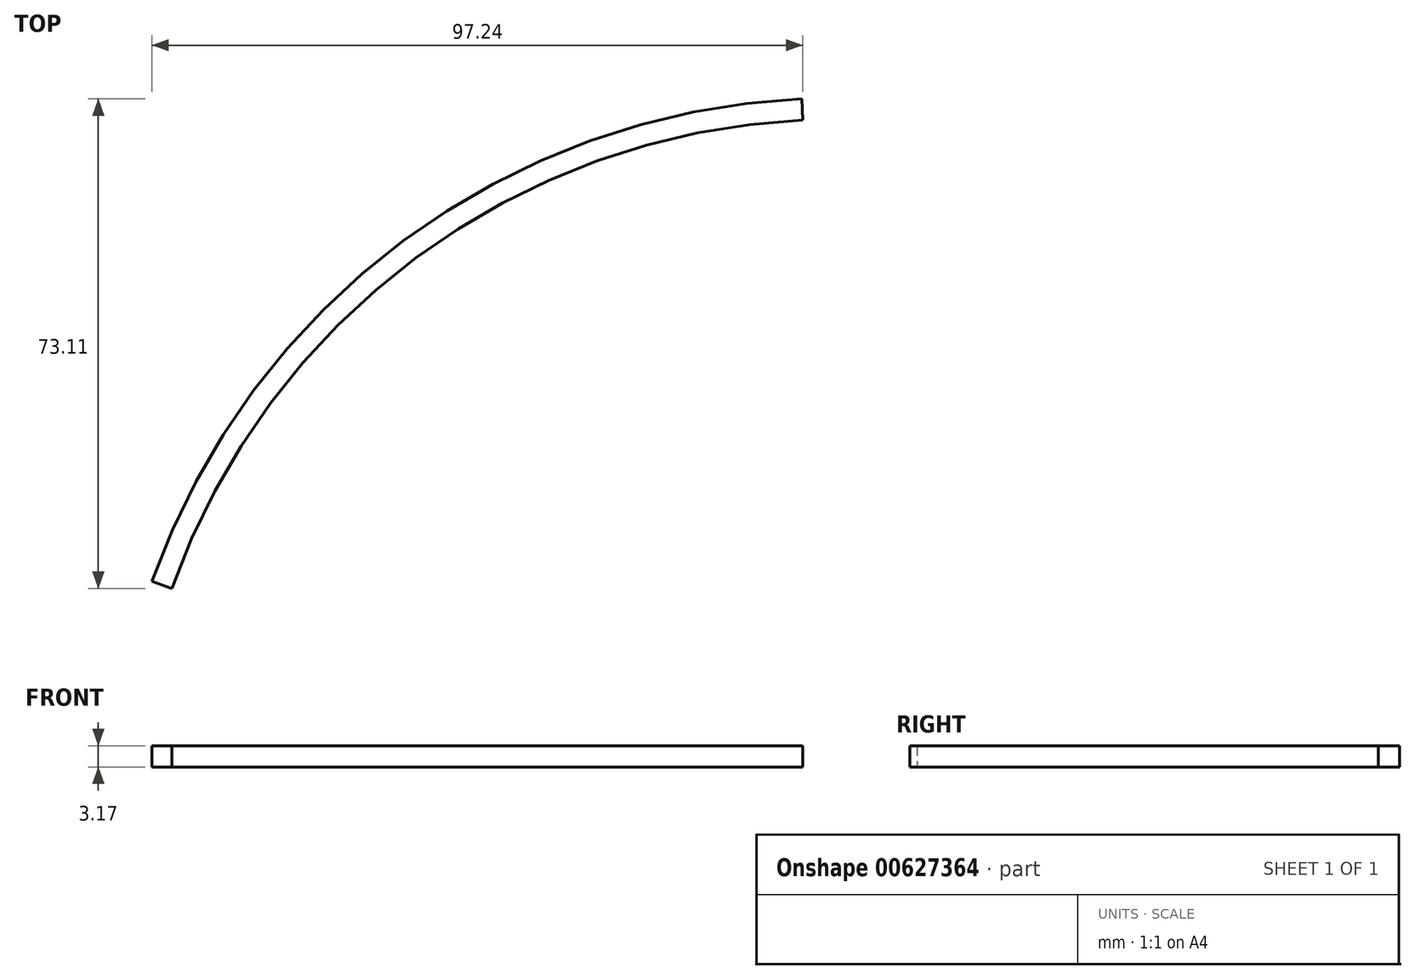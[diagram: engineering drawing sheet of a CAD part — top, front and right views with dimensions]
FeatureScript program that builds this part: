
annotation { "Feature Type Name" : "Feature", "Feature Type Description" : "" }
export const myFeature = defineFeature(function(context is Context, id is Id, definition is map)
    precondition{}
    {
        {
            var Q0;
            Q0=qCreatedBy(makeId("Top.planeOp"),FACE);
            var sketch = newSketch(context, id + "F0", { "sketchPlane" : qUnion([Q0])});
            skArc(sketch, "E0", {"start": v(-4.86, 105.02) * mm, "mid": v(-62.65, 84.42) * mm, "end": v(-99.1, 35.08) * mm});
            skArc(sketch, "E1.0", {"start": v(-5, 108.19) * mm, "mid": v(-64.54, 86.97) * mm, "end": v(-102.1, 36.14) * mm});
            skLineSegment(sketch, "E2", {"start": v(-102.1, 36.14) * mm, "end": v(-99.1, 35.08) * mm});
            skLineSegment(sketch, "E3", {"start": v(-4.86, 105.02) * mm, "end": v(-5, 108.19) * mm});
            skSolve(sketch);
        }
        {
            var Q0;
            Q0=makeQuery(id+"F0.imprint","IMPRINT",FACE,{"disambiguationData":[TD([[makeQuery(id+"F0.imprint","IMPRINT",EDGE,{"derivedFrom":sQuery(id+"F0.wireOp",EDGE,"E0")}),-1.0]])]});
            extrude(context, id + "F1", {"entities" : qUnion([Q0]), "depth" : 3.17 * mm, "offsetDistance" : 25.4 * mm});
        }
    });
